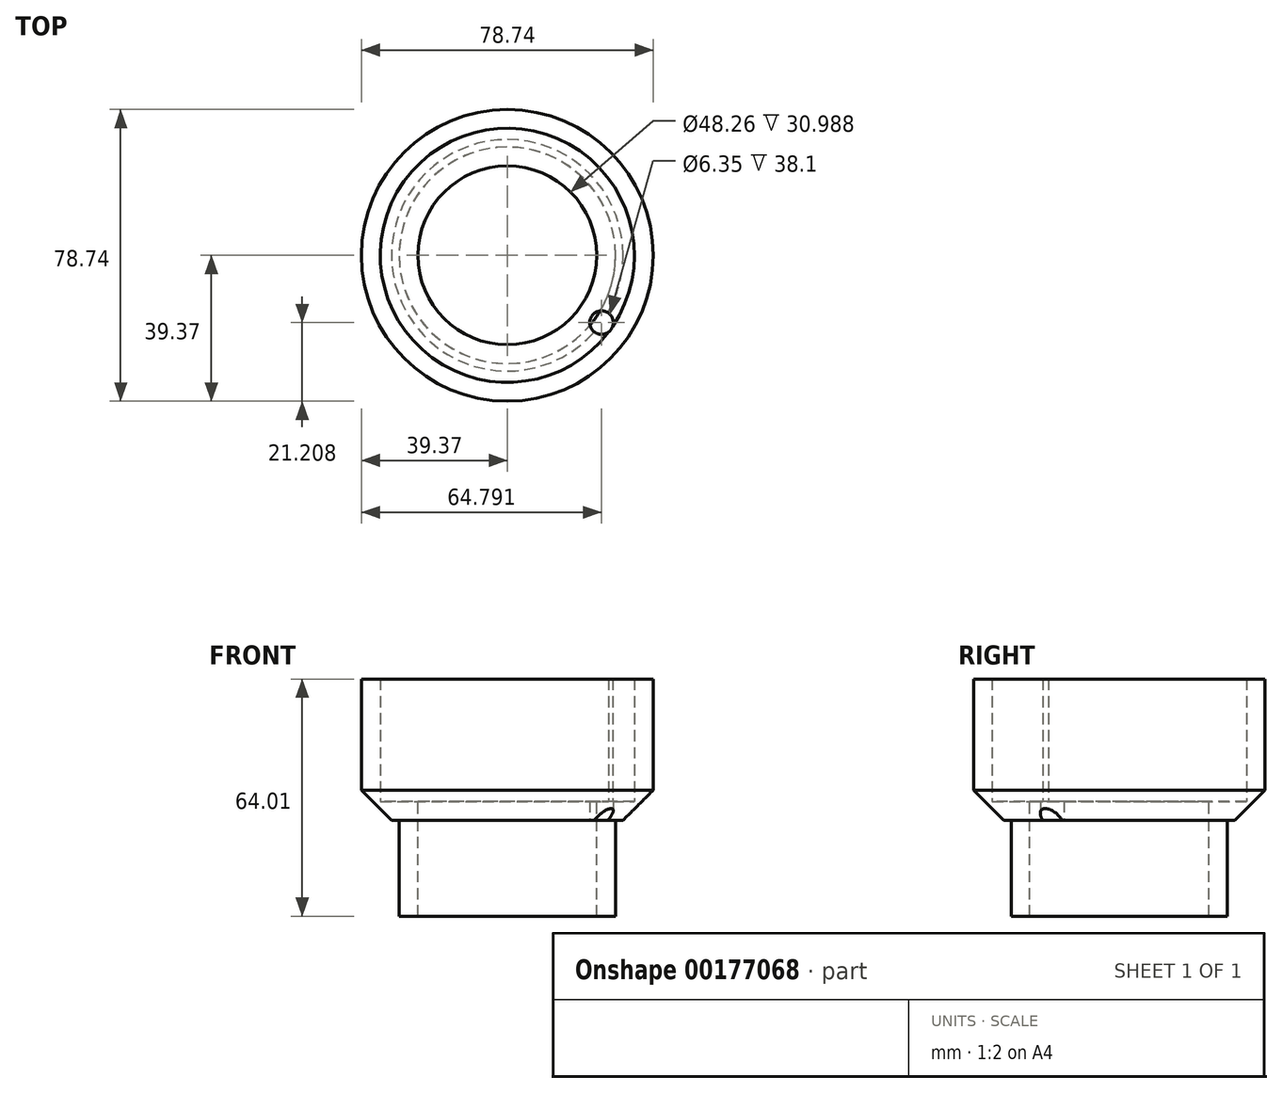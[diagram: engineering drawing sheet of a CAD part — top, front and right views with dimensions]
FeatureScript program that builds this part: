
annotation { "Feature Type Name" : "Feature", "Feature Type Description" : "" }
export const myFeature = defineFeature(function(context is Context, id is Id, definition is map)
    precondition{}
    {
        {
            var Q0;
            Q0=qCreatedBy(makeId("Top.planeOp"),FACE);
            var sketch = newSketch(context, id + "F0", { "sketchPlane" : qUnion([Q0])});
            skCircle(sketch, "E0", {"center": v(0, 0) * mm, "radius": 29.2 * mm});
            skSolve(sketch);
        }
        {
            var Q0;
            Q0=makeQuery(id+"F0.imprint","IMPRINT",FACE,{"disambiguationData":[TD([[makeQuery(id+"F0.imprint","IMPRINT",EDGE,{"derivedFrom":sQuery(id+"F0.wireOp",EDGE,"E0")}),1.0]])]});
            extrude(context, id + "F1", {"entities" : qUnion([Q0]), "oppositeDirection" : true, "depth" : 25.9 * mm});
        }
        {
            var Q0;
            Q0=qCreatedBy(makeId("Top.planeOp"),FACE);
            var sketch = newSketch(context, id + "F2", { "sketchPlane" : qUnion([Q0])});
            skCircle(sketch, "E1", {"center": v(0, 0) * mm, "radius": 39.37 * mm});
            skSolve(sketch);
        }
        {
            var Q0;
            Q0=makeQuery(id+"F2.imprint","IMPRINT",FACE,{"disambiguationData":[TD([[makeQuery(id+"F2.imprint","IMPRINT",EDGE,{"derivedFrom":sQuery(id+"F2.wireOp",EDGE,"E1")}),1.0]])]});
            extrude(context, id + "F3", {"entities" : qUnion([Q0]), "operationType" : NewBodyOperationType.ADD, "depth" : 38.1 * mm});
        }
        {
            var Q0;
            Q0=makeQuery(id+"F3.opExtrude","CAP_FACE",FACE,{"disambiguationData":[OSD([sQuery(id+"F2.wireOp",EDGE,"E1")])],"isStart":false});
            var Q1;
            Q1=makeQuery(id+"F1.opExtrude","CAP_FACE",FACE,{"disambiguationData":[OSD([sQuery(id+"F0.wireOp",EDGE,"E0")])],"isStart":false});
            shell(context, id + "F4", {"entities" : qUnion([Q0, Q1]), "thickness" : 5.08 * mm});
        }
        {
            var Q0;
            Q0=makeQuery(id+"F3.opExtrude","CAP_EDGE",EDGE,{"disambiguationData":[OSD([sQuery(id+"F2.wireOp",EDGE,"E1")])],"isStart":true});
            chamfer(context, id + "F5", {"entities" : qUnion([Q0]), "width" : 8.13 * mm, "tangentPropagation" : true});
        }
        {
            var Q0;
            Q0=makeQuery(id+"F3.opExtrude","CAP_FACE",FACE,{"disambiguationData":[OSD([sQuery(id+"F2.wireOp",EDGE,"E1")])],"isStart":true});
            var sketch = newSketch(context, id + "F6", { "sketchPlane" : qUnion([Q0])});
            skPoint(sketch, "E2", {"position": v(25.42, 18.16) * mm});
            skSolve(sketch);
        }
        {
            var Q0;
            Q0=sQuery(id+"F6.wireOp",VERTEX,"E2");
            var Q1;
            Q1=makeQuery(id+"F1.opExtrude","SWEPT_BODY",BODY,{"disambiguationData":[OSD([sQuery(id+"F0.wireOp",EDGE,"E0")])]});
            hole(context, id + "F7", {"style" : HoleStyle.SIMPLE, "endStyle" : HoleEndStyle.THROUGH, "holeDiameter" : 6.35 * mm, "locations" : qUnion([Q0]), "scope" : qUnion([Q1]), "isTappedThrough" : true});
        }
    });
